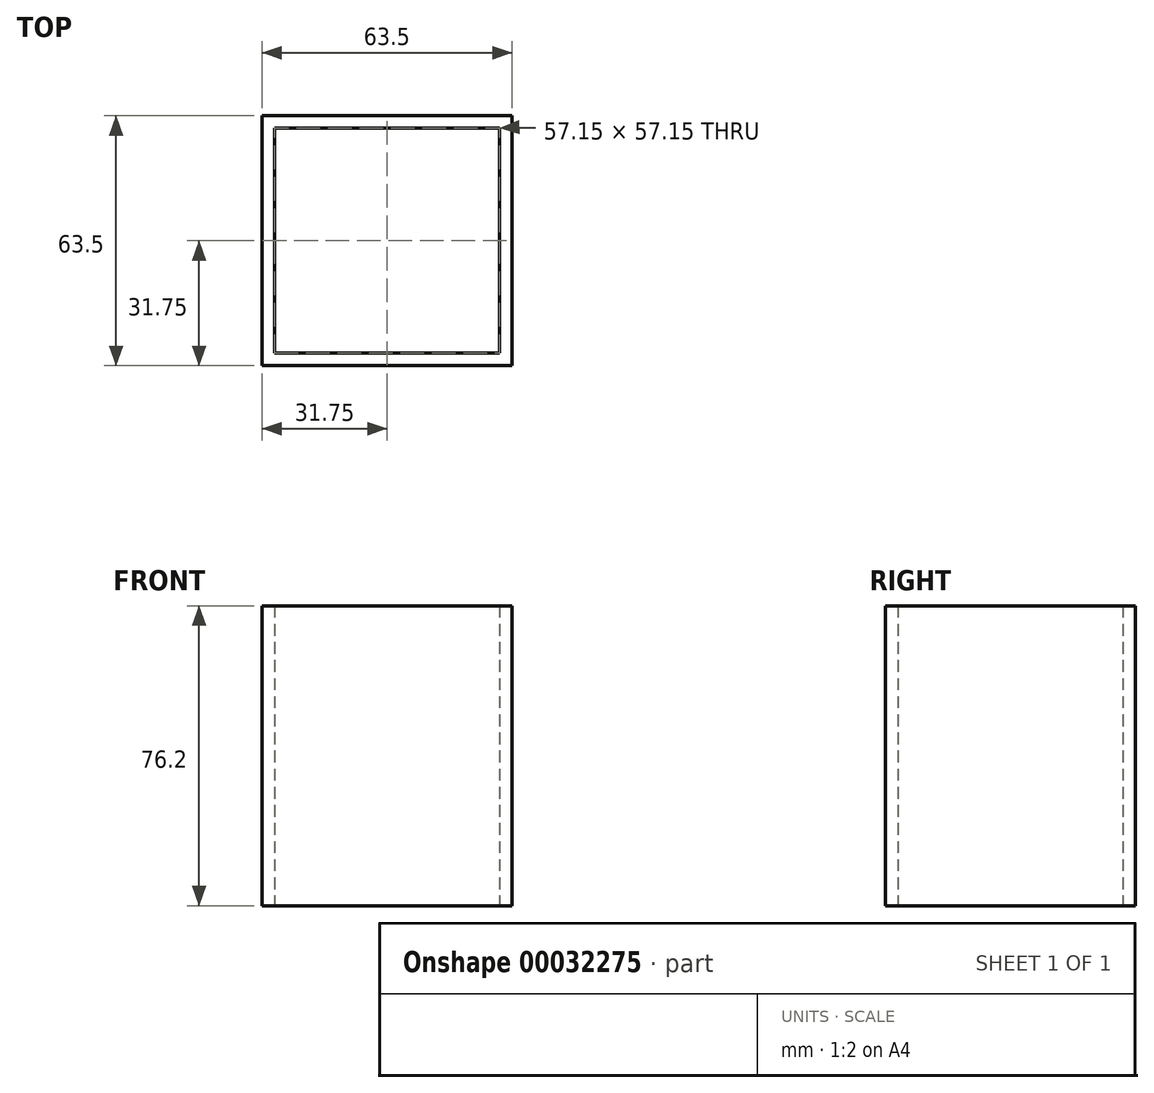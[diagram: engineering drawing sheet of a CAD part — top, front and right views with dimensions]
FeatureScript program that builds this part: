
annotation { "Feature Type Name" : "Feature", "Feature Type Description" : "" }
export const myFeature = defineFeature(function(context is Context, id is Id, definition is map)
    precondition{}
    {
        {
            var Q0;
            Q0=qCreatedBy(makeId("Top.planeOp"),FACE);
            var sketch = newSketch(context, id + "F0", { "sketchPlane" : qUnion([Q0])});
            skLineSegment(sketch, "E0.bottom", {"start": v(0, 0) * mm, "end": v(-63.5, 0) * mm});
            skLineSegment(sketch, "E0.top", {"start": v(0, 63.5) * mm, "end": v(-63.5, 63.5) * mm});
            skLineSegment(sketch, "E0.left", {"start": v(0, 0) * mm, "end": v(0, 63.5) * mm});
            skLineSegment(sketch, "E0.right", {"start": v(-63.5, 0) * mm, "end": v(-63.5, 63.5) * mm});
            skLineSegment(sketch, "E1.bottom", {"start": v(-60.33, 60.32) * mm, "end": v(-3.18, 60.33) * mm});
            skLineSegment(sketch, "E1.top", {"start": v(-60.33, 3.17) * mm, "end": v(-3.17, 3.18) * mm});
            skLineSegment(sketch, "E1.left", {"start": v(-60.33, 60.32) * mm, "end": v(-60.33, 3.17) * mm});
            skLineSegment(sketch, "E1.right", {"start": v(-3.18, 60.33) * mm, "end": v(-3.17, 3.18) * mm});
            skSolve(sketch);
        }
        {
            var Q0;
            Q0=makeQuery(id+"F0.imprint","IMPRINT",FACE,{"disambiguationData":[TD([[makeQuery(id+"F0.imprint","IMPRINT",EDGE,{"derivedFrom":sQuery(id+"F0.wireOp",EDGE,"E0.bottom")}),-1.0]])]});
            extrude(context, id + "F1", {"entities" : qUnion([Q0]), "depth" : 76.2 * mm});
        }
    });
